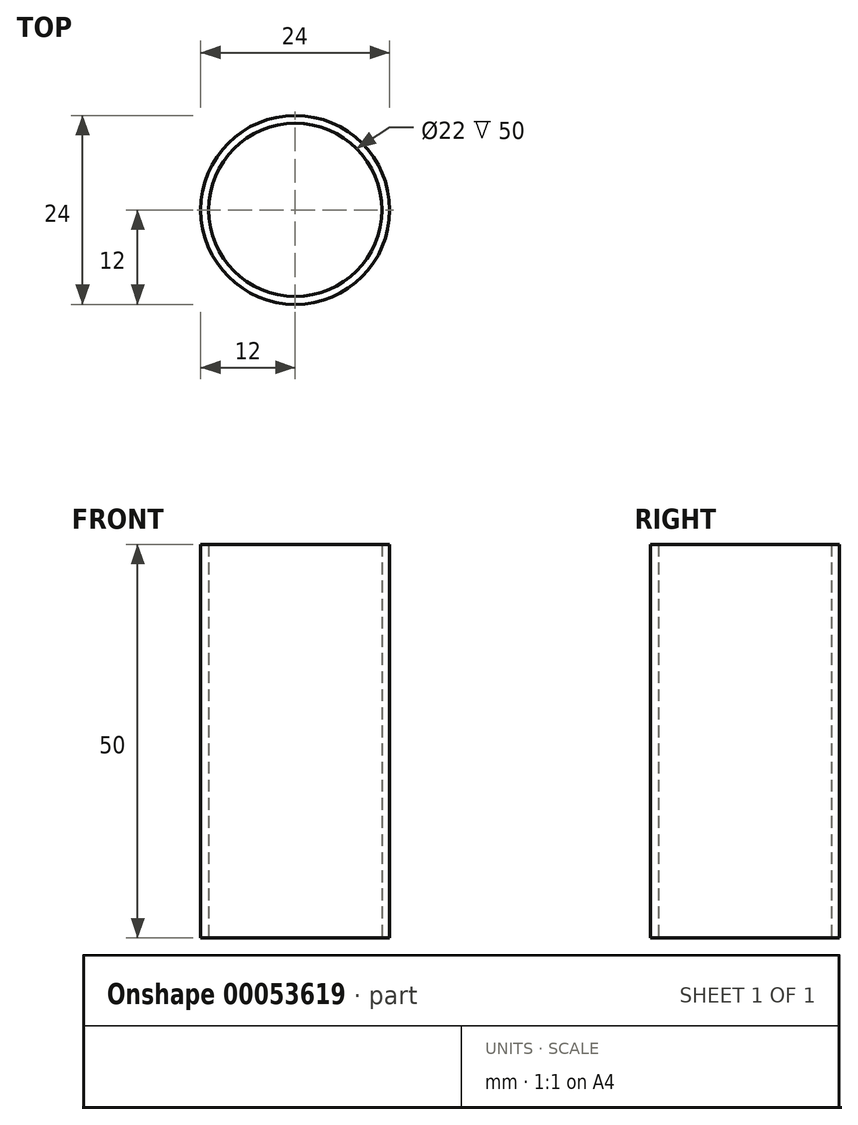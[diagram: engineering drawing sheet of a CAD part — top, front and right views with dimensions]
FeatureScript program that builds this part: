
annotation { "Feature Type Name" : "Feature", "Feature Type Description" : "" }
export const myFeature = defineFeature(function(context is Context, id is Id, definition is map)
    precondition{}
    {
        {
            var Q0;
            Q0=qCreatedBy(makeId("Top.planeOp"),FACE);
            var sketch = newSketch(context, id + "F0", { "sketchPlane" : qUnion([Q0])});
            skCircle(sketch, "E0", {"center": v(0, 0) * mm, "radius": 11 * mm});
            skCircle(sketch, "E1", {"center": v(0, 0) * mm, "radius": 12 * mm});
            skSolve(sketch);
        }
        {
            var Q0;
            Q0=makeQuery(id+"F0.imprint","IMPRINT",FACE,{"disambiguationData":[TD([[makeQuery(id+"F0.imprint","IMPRINT",EDGE,{"derivedFrom":sQuery(id+"F0.wireOp",EDGE,"E0")}),-1.0]])]});
            extrude(context, id + "F1", {"entities" : qUnion([Q0]), "depth" : 50 * mm});
        }
    });
